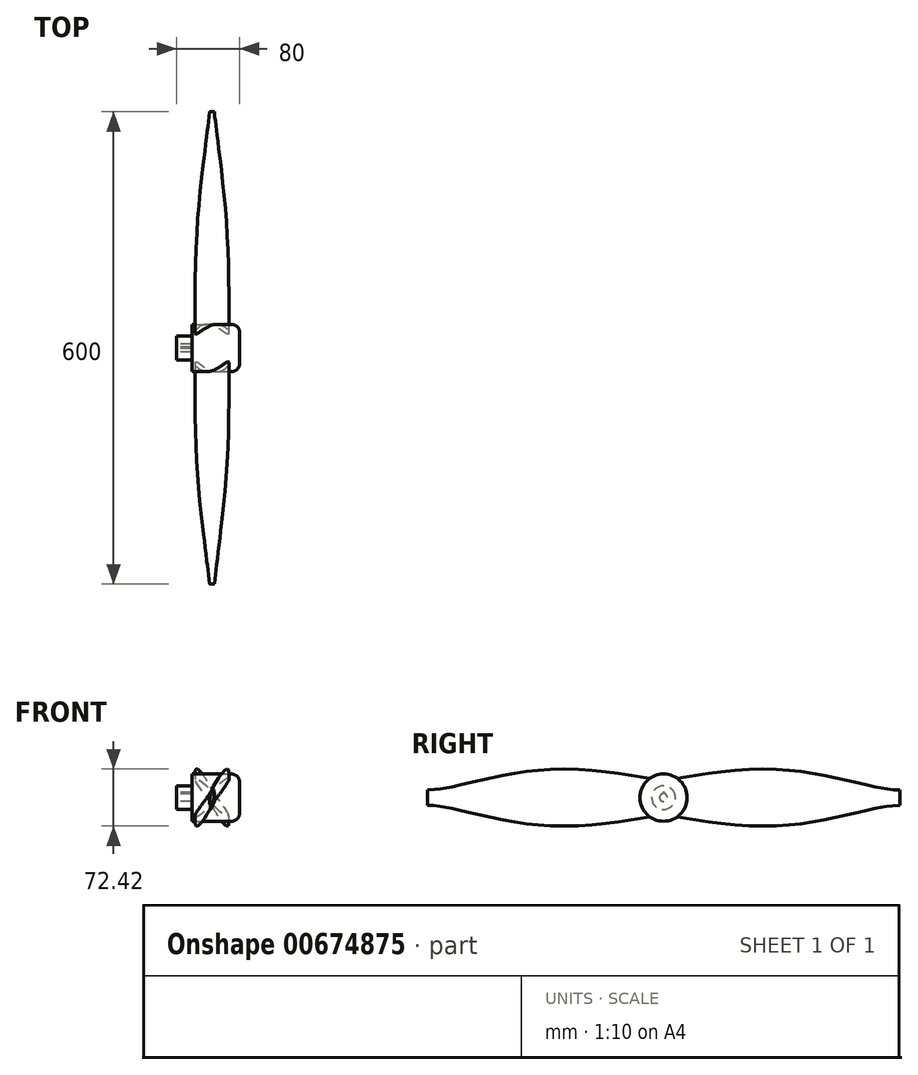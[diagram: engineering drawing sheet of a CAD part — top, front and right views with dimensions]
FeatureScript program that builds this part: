
annotation { "Feature Type Name" : "Feature", "Feature Type Description" : "" }
export const myFeature = defineFeature(function(context is Context, id is Id, definition is map)
    precondition{}
    {
        {
            var Q0;
            Q0=qCreatedBy(makeId("Front.planeOp"),FACE);
            var sketch = newSketch(context, id + "F0", { "sketchPlane" : qUnion([Q0])});
            skEllipse(sketch, "E0", {"center": v(0, 0) * mm, "majorRadius": 30 * mm, "minorRadius": 5 * mm, "majorAxis": v(0.7, 0.7)});
            skLineSegment(sketch, "E1", {"start": v(21.21, 21.21) * mm, "end": v(-21.21, -21.21) * mm, "construction": true});
            skLineSegment(sketch, "E2", {"start": v(-3.54, 3.54) * mm, "end": v(3.54, -3.54) * mm, "construction": true});
            skSolve(sketch);
        }
        {
            assignVariable(context, id + "F1", {"name" : "Amplitude", "anyValue" : 300});
        }
        {
            var Q0;
            Q0=qCreatedBy(makeId("Front.planeOp"),FACE);
            cPlane(context, id + "F2", {"entities" : qUnion([Q0]), "cplaneType" : CPlaneType.OFFSET, "offset" : (getVariable(context, 'Amplitude') / 2) * mm, "width" : 150 * mm, "height" : 150 * mm});
        }
        {
            var Q0;
            Q0=qCreatedBy(id+"F2.planeOp",FACE);
            var sketch = newSketch(context, id + "F3", { "sketchPlane" : qUnion([Q0])});
            skEllipse(sketch, "E3", {"center": v(0, 0) * mm, "majorRadius": 40 * mm, "minorRadius": 5 * mm, "majorAxis": v(0.46, 0.89)});
            skLineSegment(sketch, "E4", {"start": v(-18.47, -35.48) * mm, "end": v(18.47, 35.48) * mm, "construction": true});
            skLineSegment(sketch, "E5", {"start": v(-4.44, 2.3) * mm, "end": v(4.44, -2.3) * mm, "construction": true});
            skSolve(sketch);
        }
        {
            var Q0;
            Q0=qCreatedBy(makeId("Front.planeOp"),FACE);
            cPlane(context, id + "F4", {"entities" : qUnion([Q0]), "cplaneType" : CPlaneType.OFFSET, "offset" : (getVariable(context, 'Amplitude')) * mm, "width" : 150 * mm, "height" : 150 * mm});
        }
        {
            var Q0;
            Q0=qCreatedBy(id+"F4.planeOp",FACE);
            var sketch = newSketch(context, id + "F5", { "sketchPlane" : qUnion([Q0])});
            skEllipse(sketch, "E6", {"center": v(0, 0) * mm, "majorRadius": 10 * mm, "minorRadius": 2.5 * mm, "majorAxis": v(0.17, 0.98)});
            skLineSegment(sketch, "E7", {"start": v(1.74, 9.85) * mm, "end": v(-1.74, -9.85) * mm});
            skLineSegment(sketch, "E8", {"start": v(-2.46, 0.43) * mm, "end": v(2.46, -0.43) * mm, "construction": true});
            skSolve(sketch);
        }
        {
            var Q0;
            Q0 = qSketchRegion(id + "F0", true);
            var Q1;
            Q1 = qSketchRegion(id + "F3", true);
            var Q2;
            Q2 = qSketchRegion(id + "F5", true);
            loft(context, id + "F6", {"sheetProfilesArray" : [{ "sheetProfileEntities" : qUnion([Q0]) }, { "sheetProfileEntities" : qUnion([Q1]) }, { "sheetProfileEntities" : qUnion([Q2]) }]});
        }
        {
            var Q0;
            Q0=qCreatedBy(makeId("Front.planeOp"),FACE);
            var sketch = newSketch(context, id + "F7", { "sketchPlane" : qUnion([Q0])});
            skLineSegment(sketch, "E9", {"start": v(-111.23, 0) * mm, "end": v(103.3, 0) * mm, "construction": true});
            skSolve(sketch);
        }
        {
            var Q0;
            {var subQ0=sQuery(id+"F5.wireOp",EDGE,"E7");Q0=makeQuery(id+"F6.opLoft","SWEPT_BODY",BODY,{"disambiguationData":[OSD([makeQuery(id+"F0.imprint","IMPRINT",FACE,{"disambiguationData":[TD([[makeQuery(id+"F0.imprint","IMPRINT",EDGE,{"derivedFrom":sQuery(id+"F0.wireOp",EDGE,"E0")}),1.0]])]}),sQuery(id+"F3.wireOp",EDGE,"E3"),makeQuery(id+"F5.imprint","IMPRINT",FACE,{"disambiguationData":[TD([[makeQuery(id+"F5.imprint","IMPRINT",EDGE,{"derivedFrom":subQ0}),-1.0]])]})])]});}
            var Q1;
            Q1=sQuery(id+"F7.wireOp",EDGE,"E9");
            circularPattern(context, id + "F8", {"entities" : qUnion([Q0]), "axis" : qUnion([Q1]), "angle" : 360 * degree, "instanceCount" : 2, "equalSpace" : true});
        }
        {
            var Q0;
            Q0=qCreatedBy(makeId("Front.planeOp"),FACE);
            var sketch = newSketch(context, id + "F9", { "sketchPlane" : qUnion([Q0])});
            skLineSegment(sketch, "E10", {"start": v(-45, 0) * mm, "end": v(-45, 15) * mm});
            skLineSegment(sketch, "E11", {"start": v(-45, 15) * mm, "end": v(-25, 15) * mm});
            skLineSegment(sketch, "E12", {"start": v(-25, 15) * mm, "end": v(-25, 30) * mm});
            skLineSegment(sketch, "E13", {"start": v(-25, 30) * mm, "end": v(35, 30) * mm});
            skLineSegment(sketch, "E14", {"start": v(35, 30) * mm, "end": v(35, 0) * mm});
            skLineSegment(sketch, "E15", {"start": v(35, 0) * mm, "end": v(-45, 0) * mm});
            skLineSegment(sketch, "E16", {"start": v(55.43, 0) * mm, "end": v(-59.97, 0) * mm, "construction": true});
            skSolve(sketch);
        }
        {
            var Q0;
            Q0 = qSketchRegion(id + "F9", true);
            var Q1;
            Q1=sQuery(id+"F9.wireOp",EDGE,"E16");
            revolve(context, id + "F10", {"operationType" : NewBodyOperationType.ADD, "entities" : qUnion([Q0]), "axis" : qUnion([Q1]), "revolveType" : RevolveType.FULL});
        }
        {
            var Q0;
            Q0=makeQuery(id+"F10.opRevolve","SWEPT_EDGE",EDGE,{"disambiguationData":[OSD([sQuery(id+"F9.wireOp",EDGE,"E13"),sQuery(id+"F9.wireOp",EDGE,"E14")])]});
            fillet(context, id + "F11", {"entities" : qUnion([Q0]), "radius" : 10 * mm, "tangentPropagation" : true, "allowEdgeOverflow" : false});
        }
        {
            var Q0;
            Q0=makeQuery(id+"F10.opRevolve","SWEPT_FACE",FACE,{"disambiguationData":[OSD([sQuery(id+"F9.wireOp",EDGE,"E10")])]});
            var sketch = newSketch(context, id + "F12", { "sketchPlane" : qUnion([Q0])});
            skArc(sketch, "E17", {"start": v(-1, 4.9) * mm, "mid": v(0, -5) * mm, "end": v(1, 4.9) * mm});
            skLineSegment(sketch, "E18.bottom", {"start": v(-1, 6.9) * mm, "end": v(1, 6.9) * mm});
            skLineSegment(sketch, "E18.left", {"start": v(-1, 6.9) * mm, "end": v(-1, 4.9) * mm});
            skLineSegment(sketch, "E18.right", {"start": v(1, 6.9) * mm, "end": v(1, 4.9) * mm});
            skSolve(sketch);
        }
        {
            var Q0;
            Q0 = qSketchRegion(id + "F12", true);
            extrude(context, id + "F13", {"entities" : qUnion([Q0]), "operationType" : NewBodyOperationType.REMOVE, "oppositeDirection" : true, "depth" : 20 * mm, "offsetDistance" : 25 * mm});
        }
    });
